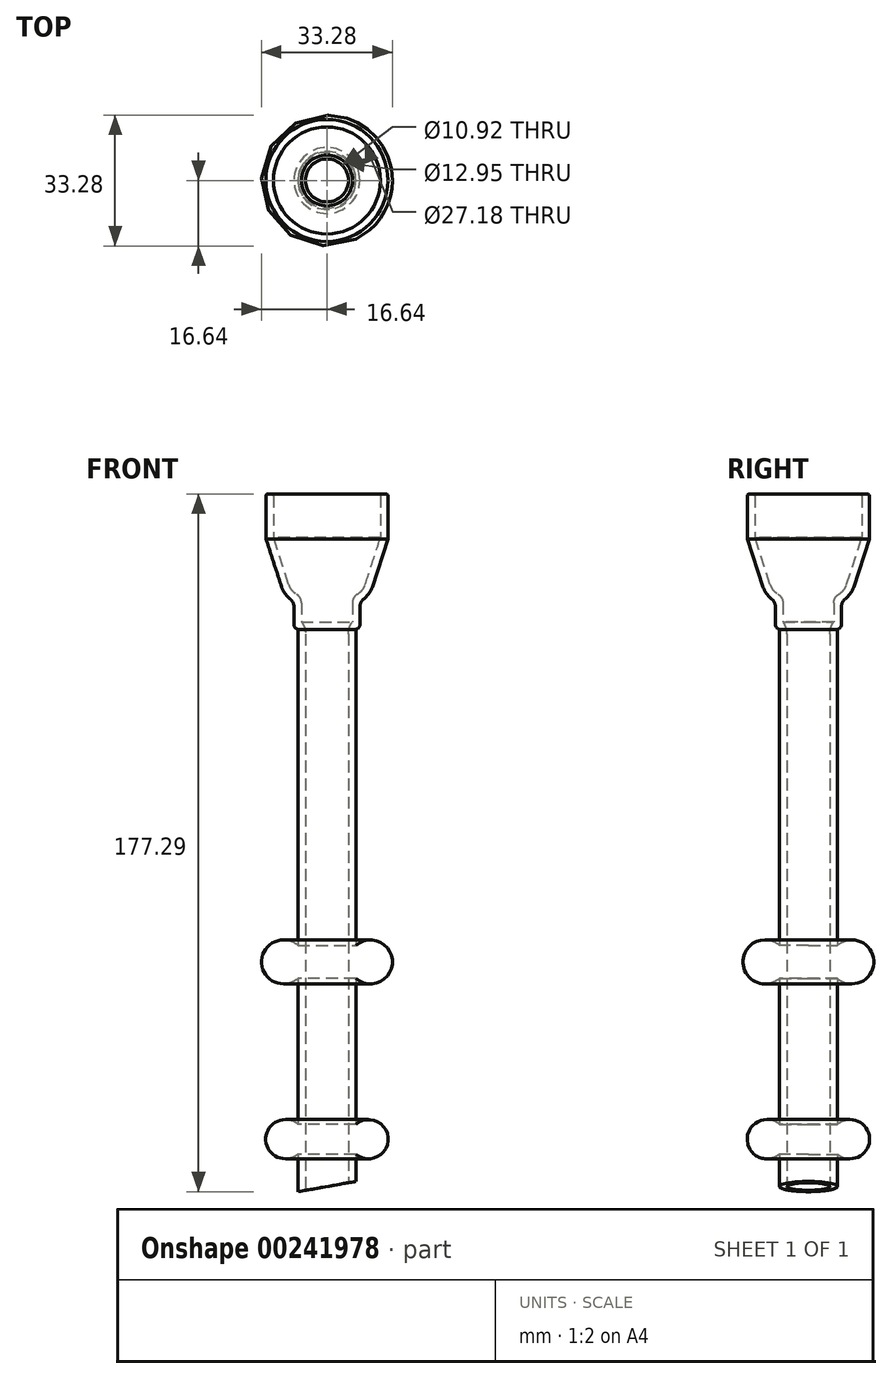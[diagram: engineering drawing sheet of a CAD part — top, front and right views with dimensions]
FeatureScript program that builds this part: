
annotation { "Feature Type Name" : "Feature", "Feature Type Description" : "" }
export const myFeature = defineFeature(function(context is Context, id is Id, definition is map)
    precondition{}
    {
        {
            var Q0;
            Q0=qCreatedBy(makeId("Front.planeOp"),FACE);
            cPlane(context, id + "F0", {"entities" : qUnion([Q0]), "cplaneType" : CPlaneType.OFFSET, "offset" : 25.4 * mm, "width" : 152.4 * mm, "height" : 152.4 * mm});
        }
        {
            var Q0;
            Q0=qCreatedBy(makeId("Front.planeOp"),FACE);
            cPlane(context, id + "F1", {"entities" : qUnion([Q0]), "cplaneType" : CPlaneType.OFFSET, "offset" : 10.15 * mm, "width" : 152.4 * mm, "height" : 152.4 * mm});
        }
        {
            var Q0;
            Q0=qCreatedBy(makeId("Front.planeOp"),FACE);
            var sketch = newSketch(context, id + "F2", { "sketchPlane" : qUnion([Q0])});
            skLineSegment(sketch, "E0", {"start": v(0, -127) * mm, "end": v(0, 127) * mm, "construction": true});
            skLineSegment(sketch, "E1", {"start": v(0, 0) * mm, "end": v(7.37, 0) * mm, "construction": true});
            skPoint(sketch, "E1.endSnap0", {"position": v(0, 0) * mm});
            skLineSegment(sketch, "E2", {"start": v(7.37, -71.44) * mm, "end": v(7.37, 71.44) * mm});
            skLineSegment(sketch, "E3", {"start": v(7.37, 71.44) * mm, "end": v(8.38, 71.44) * mm});
            skLineSegment(sketch, "E4", {"start": v(8.38, 71.44) * mm, "end": v(8.38, 78.55) * mm});
            skLineSegment(sketch, "E5", {"start": v(7.37, -71.44) * mm, "end": v(0, -71.44) * mm});
            skLineSegment(sketch, "E6", {"start": v(0, 94.42) * mm, "end": v(15.5, 94.42) * mm, "construction": true});
            skLineSegment(sketch, "E7", {"start": v(15.5, 94.42) * mm, "end": v(11.54, 82.24) * mm});
            skArc(sketch, "E8", {"start": v(11.54, 82.24) * mm, "mid": v(10.33, 80.08) * mm, "end": v(8.38, 78.55) * mm});
            skLineSegment(sketch, "E9", {"start": v(15.5, 94.42) * mm, "end": v(15.5, 105.85) * mm});
            skLineSegment(sketch, "E10", {"start": v(15.5, 105.85) * mm, "end": v(0, 105.85) * mm});
            skLineSegment(sketch, "E11", {"start": v(0, -71.44) * mm, "end": v(0, 105.85) * mm});
            skSolve(sketch);
        }
        {
            var Q0;
            Q0 = qSketchRegion(id + "F2", true);
            var Q1;
            Q1=sQuery(id+"F2.wireOp",EDGE,"E11");
            revolve(context, id + "F3", {"entities" : qUnion([Q0]), "axis" : qUnion([Q1]), "revolveType" : RevolveType.FULL});
        }
        {
            var Q0;
            Q0=qCreatedBy(makeId("Front.planeOp"),FACE);
            var sketch = newSketch(context, id + "F4", { "sketchPlane" : qUnion([Q0])});
            skLineSegment(sketch, "E12", {"start": v(-7.37, -71.44) * mm, "end": v(7.87, -68.75) * mm});
            skLineSegment(sketch, "E13", {"start": v(7.87, -68.75) * mm, "end": v(7.87, -71.44) * mm});
            skLineSegment(sketch, "E14", {"start": v(7.87, -71.44) * mm, "end": v(-7.37, -71.44) * mm});
            skSolve(sketch);
        }
        {
            var Q0;
            Q0 = qSketchRegion(id + "F4", true);
            extrude(context, id + "F5", {"entities" : qUnion([Q0]), "operationType" : NewBodyOperationType.REMOVE, "endBound" : BoundingType.THROUGH_ALL, "oppositeDirection" : true, "depth" : 25.4 * mm, "hasSecondDirection" : true, "secondDirectionBound" : SecondDirectionBoundingType.THROUGH_ALL, "secondDirectionOppositeDirection" : false, "secondDirectionDepth" : 25.4 * mm});
        }
        {
            var Q0;
            Q0=qCreatedBy(id+"F0.planeOp",FACE);
            var sketch = newSketch(context, id + "F6", { "sketchPlane" : qUnion([Q0])});
            skLineSegment(sketch, "E15", {"start": v(0, 0) * mm, "end": v(0, 146.1) * mm, "construction": true});
            skCircle(sketch, "E16", {"center": v(0, 80.78) * mm, "radius": 5.8 * mm});
            skPoint(sketch, "E17", {"position": v(0, 75) * mm});
            skSolve(sketch);
        }
        {
            var Q0;
            Q0=makeQuery(id+"FToHk4ieiOrOthV_1.boolean.opBoolean","COPY",FACE,{"derivedFrom":makeQuery(id+"FToHk4ieiOrOthV_1.opExtrude","SWEPT_FACE",FACE,{"disambiguationData":[OSD([sQuery(id+"F4.wireOp",EDGE,"E12")])]})});
            var Q1;
            Q1=makeQuery(id+"F3.opRevolve","SWEPT_FACE",FACE,{"disambiguationData":[OSD([sQuery(id+"F2.wireOp",EDGE,"E10")])]});
            var Q2;
            Q2=makeQuery(id+"F5.boolean.opBoolean","COPY",FACE,{"derivedFrom":makeQuery(id+"F5.opExtrude","SWEPT_FACE",FACE,{"disambiguationData":[OSD([sQuery(id+"F4.wireOp",EDGE,"E12")])]})});
            shell(context, id + "F7", {"entities" : qUnion([Q0, Q1, Q2]), "thickness" : 1.9 * mm});
        }
        {
            var Q0;
            Q0=qCreatedBy(makeId("Front.planeOp"),FACE);
            var sketch = newSketch(context, id + "F8", { "sketchPlane" : qUnion([Q0])});
            skLineSegment(sketch, "E18", {"start": v(-38.19, -58.1) * mm, "end": v(38.19, -58.1) * mm, "construction": true});
            skPoint(sketch, "E19", {"position": v(0, -58.1) * mm});
            skLineSegment(sketch, "E20", {"start": v(0, 0) * mm, "end": v(0, -97.56) * mm, "construction": true});
            skLineSegment(sketch, "E21", {"start": v(7.37, -54.3) * mm, "end": v(7.37, -61.91) * mm});
            skPoint(sketch, "E22", {"position": v(7.37, -58.1) * mm});
            skLineSegment(sketch, "E23", {"start": v(0, -58.1) * mm, "end": v(7.37, -58.1) * mm, "construction": true});
            skArc(sketch, "E24", {"start": v(7.37, -61.91) * mm, "mid": v(15.56, -58.1) * mm, "end": v(7.37, -54.3) * mm});
            skPoint(sketch, "E25", {"position": v(15.56, -58.1) * mm});
            skSolve(sketch);
        }
        {
            var Q0;
            Q0 = qSketchRegion(id + "F8", true);
            var Q1;
            Q1=sQuery(id+"F8.wireOp",EDGE,"E20");
            revolve(context, id + "F9", {"operationType" : NewBodyOperationType.ADD, "entities" : qUnion([Q0]), "axis" : qUnion([Q1]), "revolveType" : RevolveType.FULL});
        }
        {
            var Q0;
            Q0=qCreatedBy(makeId("Right.planeOp"),FACE);
            var sketch = newSketch(context, id + "F10", { "sketchPlane" : qUnion([Q0])});
            skLineSegment(sketch, "E26", {"start": v(-12.94, 86.58) * mm, "end": v(-24.1, 86.58) * mm});
            skFitSpline(sketch, "E27", {"points": [v(-12.94, 86.58) * mm, v(-11.3, 84.3) * mm, v(-10.08, 82.24) * mm], "startDerivative": vector(3.69, -4.6) * mm, "endDerivative": vector(1.54, -3.1) * mm});
            skFitSpline(sketch, "E28", {"points": [v(-10.08, 82.24) * mm, v(-9.42, 81.13) * mm, v(-8.6, 80.11) * mm, v(-7.83, 79.4) * mm, v(-6.46, 78.55) * mm], "startDerivative": vector(2.38, -4.55) * mm, "endDerivative": vector(5.26, -2.5) * mm});
            skFitSpline(sketch, "E29", {"points": [v(-6.46, 78.55) * mm, v(-7.4, 76.52) * mm, v(-8.38, 75) * mm], "startDerivative": vector(-1.48, -4.16) * mm, "endDerivative": vector(-2.23, -3.16) * mm});
            skLineSegment(sketch, "E30", {"start": v(-8.38, 75) * mm, "end": v(-37.06, 75) * mm});
            skLineSegment(sketch, "E31", {"start": v(-37.06, 75) * mm, "end": v(-37.06, 86.58) * mm});
            skLineSegment(sketch, "E32", {"start": v(-37.06, 86.58) * mm, "end": v(-24.1, 86.58) * mm});
            skSolve(sketch);
        }
        {
            var Q0;
            Q0=makeQuery(id+"F7.opShell","OFFSET_EDGE",EDGE,{"disambiguationData":[OSD([sQuery(id+"F2.wireOp",EDGE,"E2"),sQuery(id+"F2.wireOp",EDGE,"E3")])]});
            fillet(context, id + "F11", {"entities" : qUnion([Q0]), "radius" : 5.08 * mm, "tangentPropagation" : true, "allowEdgeOverflow" : false});
        }
        {
            var Q0;
            Q0=makeQuery(id+"F3.opRevolve","SWEPT_EDGE",EDGE,{"disambiguationData":[OSD([sQuery(id+"F2.wireOp",EDGE,"E3"),sQuery(id+"F2.wireOp",EDGE,"E4")])]});
            fillet(context, id + "F12", {"entities" : qUnion([Q0]), "radius" : 1.27 * mm, "tangentPropagation" : true, "allowEdgeOverflow" : false});
        }
        {
            var Q0;
            Q0=makeQuery(id+"F3.opRevolve","SWEPT_EDGE",EDGE,{"disambiguationData":[OSD([sQuery(id+"F2.wireOp",EDGE,"E4"),sQuery(id+"F2.wireOp",EDGE,"E8")])]});
            fillet(context, id + "F13", {"entities" : qUnion([Q0]), "radius" : 2.54 * mm, "tangentPropagation" : true, "allowEdgeOverflow" : false});
        }
        {
            var Q0;
            Q0=makeQuery(id+"F7.opShell","OFFSET_EDGE",EDGE,{"disambiguationData":[OSD([sQuery(id+"F2.wireOp",EDGE,"E4"),sQuery(id+"F2.wireOp",EDGE,"E8")])]});
            fillet(context, id + "F14", {"entities" : qUnion([Q0]), "radius" : 2.54 * mm, "tangentPropagation" : true, "allowEdgeOverflow" : false});
        }
        {
            var Q0;
            Q0=makeQuery(id+"F7.opShell","OFFSET_EDGE",EDGE,{"disambiguationData":[OSD([sQuery(id+"F2.wireOp",EDGE,"E9"),sQuery(id+"F2.wireOp",EDGE,"E10")])]});
            var Q1;
            Q1=makeQuery(id+"F3.opRevolve","SWEPT_EDGE",EDGE,{"disambiguationData":[OSD([sQuery(id+"F2.wireOp",EDGE,"E9"),sQuery(id+"F2.wireOp",EDGE,"E10")])]});
            fillet(context, id + "F15", {"entities" : qUnion([Q0, Q1]), "radius" : 0.5 * mm, "tangentPropagation" : true, "allowEdgeOverflow" : false});
        }
        {
            var Q0;
            Q0=qCreatedBy(makeId("Front.planeOp"),FACE);
            var sketch = newSketch(context, id + "F16", { "sketchPlane" : qUnion([Q0])});
            skLineSegment(sketch, "E33", {"start": v(0, 0) * mm, "end": v(0, -84.93) * mm, "construction": true});
            skLineSegment(sketch, "E34", {"start": v(-7.37, -13.06) * mm, "end": v(7.37, -13.06) * mm, "construction": true});
            skPoint(sketch, "E35", {"position": v(0, -13.06) * mm});
            skLineSegment(sketch, "E36", {"start": v(7.37, -8.87) * mm, "end": v(7.37, -17.25) * mm});
            skArc(sketch, "E37", {"start": v(7.37, -17.25) * mm, "mid": v(16.64, -13.06) * mm, "end": v(7.37, -8.87) * mm});
            skLineSegment(sketch, "E38", {"start": v(7.37, -13.06) * mm, "end": v(16.64, -13.06) * mm, "construction": true});
            skSolve(sketch);
        }
        {
            var Q0;
            Q0 = qSketchRegion(id + "F16", true);
            var Q1;
            Q1=sQuery(id+"F16.wireOp",EDGE,"E33");
            revolve(context, id + "F17", {"operationType" : NewBodyOperationType.ADD, "entities" : qUnion([Q0]), "axis" : qUnion([Q1]), "revolveType" : RevolveType.FULL});
        }
    });
